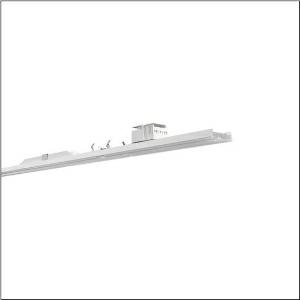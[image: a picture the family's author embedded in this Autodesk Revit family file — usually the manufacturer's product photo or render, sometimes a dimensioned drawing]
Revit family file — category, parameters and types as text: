
# Revit family: licross_r__11_recessed_ho_51tl12cn4cxld_bb0f
name_source: partatom
category: Lighting Fixtures
units: mm (PartAtom-declared; Revit-internal decimal feet)

## family parameters
Cut with Voids When Loaded = No
Host = Face
Light Source = No
Part Type = Normal
Room Calculation Point = No
Round Connector Dimension = Use Diameter
Shared = No

## types (1)
- --- (1 x LED, 3420 lm, 21.5 W, 4000K)
    Apparent Load = 22 VA
    CIE Flux Codes = 66 91 98 100 100
    Color Rendering = 80
    Color Temperature = 4000K
    Default Elevation = 1800 mm
    Description = Licross® 11 Recessed HOluminaire insert, length: 1.500mm, width: 66mm, height: 67mm, LED rated luminous flux: 12.160lm, light colour: 840, control gear: ON/OFF Multilumen, CLOi, control gear: ECG Multilumen, with plug, 6-pole, with phase selection, mains connection: 220..240V, AC/DC, 0/50..60Hz, without changeover relay, for emergency light function, for central battery installations according to DIN EN 60598-2-22, halogen-free wiring, primary optical cover: cover, of PMMA, light emission: direct distribution, protection rating (complete): IP40, insulation class (complete): insulation class I (protective earthing), certification: CE, ENEC, VDE, protection symbol: D if used in an environment without relevant dust loads with corresponding accessories, permissible ambient temperature for indoor applications: -35..+35°C, standard: EN 60598-2-22, reducing of maximum allowable ambient temperature of 5°C with ceiling mounting, corresponds to IFS (International Featured Standards) requirements for safety and quality in the food industry, packaging unit: 1 piece
    Height = 58 mm
    Lamp = 1 x LED
    Lamp Light Flux = 3420 lm
    Lamp Power = 21.5 W
    Lamp count = 1
    Length = 1500 mm
    Luminous efficacy = 159 lm/W
    Manufacturer = Siteco
    ModVariant = No
    Model = 51TL12CN4CXLD
    Mounting Place = Ceiling
    Mounting Type = Pendant
    Number of Poles = 1
    OnlyDefault = Yes
    Power Factor = 1
    Product Name = Licross® 11 Recessed HO
    Product group = luminaire insert
    ProductGroupID = 902
    Protection Class = Protection class I
    Protection Degree = IP 40
    RLX_Detail_Level = 1
    RlxData = <blob elided: 20569 chars, md5=899aefd8>
    Socket = socket
    Standby Power = 0 W
    System Light Flux = 3420 lm
    System Power = 22 W
    Type Comments = : DC mode (central or group accumulator) initial emergency light level
    Type Image = l_1266722.jpg
    URL = http://relux.com
    VarID = @adj_134287
    Voltage = 0 V
    Weight = 0.00 kg
    Width = 66 mm

## geometry (parser evidence)
native form markers: Blend x4, Sweep x10
no freeform markers — native parametric forms only
